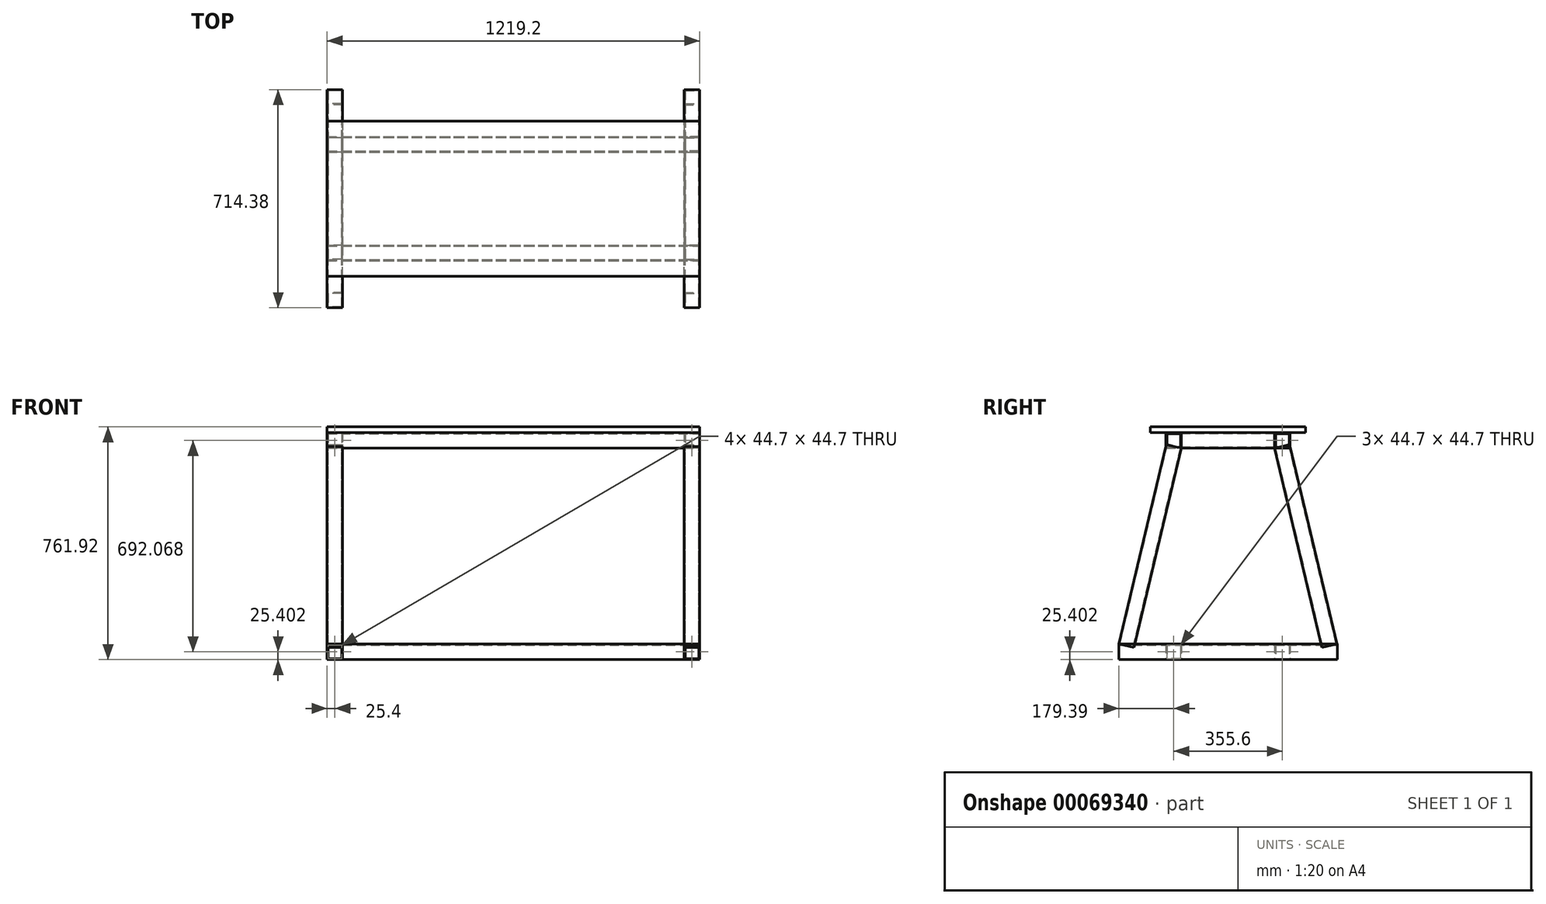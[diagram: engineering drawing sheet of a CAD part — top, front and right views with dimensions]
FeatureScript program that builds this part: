
annotation { "Feature Type Name" : "Feature", "Feature Type Description" : "" }
export const myFeature = defineFeature(function(context is Context, id is Id, definition is map)
    precondition{}
    {
        {
            var Q0;
            Q0=qCreatedBy(makeId("Top.planeOp"),FACE);
            var sketch = newSketch(context, id + "F0", { "sketchPlane" : qUnion([Q0])});
            skLineSegment(sketch, "E0.rect.bottom", {"start": v(-609.6, -254) * mm, "end": v(609.6, -254) * mm});
            skLineSegment(sketch, "E0.rect.top", {"start": v(-609.6, 254) * mm, "end": v(609.6, 254) * mm});
            skLineSegment(sketch, "E0.rect.left", {"start": v(-609.6, -254) * mm, "end": v(-609.6, 254) * mm});
            skLineSegment(sketch, "E0.rect.right", {"start": v(609.6, -254) * mm, "end": v(609.6, 254) * mm});
            skPoint(sketch, "E0.rect.middle", {"position": v(0, 0) * mm});
            skSolve(sketch);
        }
        {
            var Q0;
            Q0=makeQuery(id+"F0.imprint","IMPRINT",FACE,{"disambiguationData":[TD([[makeQuery(id+"F0.imprint","IMPRINT",EDGE,{"derivedFrom":sQuery(id+"F0.wireOp",EDGE,"E0.rect.bottom")}),1.0]])]});
            extrude(context, id + "F1", {"entities" : qUnion([Q0]), "depth" : 19.05 * mm});
        }
        {
            var Q0;
            Q0=makeQuery(id+"F1.opExtrude","SWEPT_FACE",FACE,{"disambiguationData":[OSD([sQuery(id+"F0.wireOp",EDGE,"E0.rect.right")])]});
            var Q1;
            Q1=makeQuery(id+"F1.opExtrude","SWEPT_FACE",FACE,{"disambiguationData":[OSD([sQuery(id+"F0.wireOp",EDGE,"E0.rect.right")])]});
            var sketch = newSketch(context, id + "F2", { "sketchPlane" : qUnion([Q0, Q1])});
            skPoint(sketch, "E1", {"position": v(-177.8, -25.4) * mm});
            skLineSegment(sketch, "E2.rect.bottom", {"start": v(-203.2, 0) * mm, "end": v(-152.4, 0) * mm});
            skLineSegment(sketch, "E2.rect.top", {"start": v(-203.2, -50.8) * mm, "end": v(-152.4, -50.8) * mm});
            skLineSegment(sketch, "E2.rect.right", {"start": v(-152.4, 0) * mm, "end": v(-152.4, -50.8) * mm});
            skLineSegment(sketch, "E3.rect.bottom", {"start": v(-200.15, -3.05) * mm, "end": v(-155.45, -3.05) * mm});
            skLineSegment(sketch, "E3.rect.top", {"start": v(-200.15, -47.75) * mm, "end": v(-155.45, -47.75) * mm});
            skLineSegment(sketch, "E3.rect.left", {"start": v(-200.15, -3.05) * mm, "end": v(-200.15, -47.75) * mm});
            skLineSegment(sketch, "E3.rect.right", {"start": v(-155.45, -3.05) * mm, "end": v(-155.45, -47.75) * mm});
            skLineSegment(sketch, "E4", {"start": v(0, 0) * mm, "end": v(0, -111.65) * mm});
            skLineSegment(sketch, "E5", {"start": v(-203.2, 0) * mm, "end": v(-203.2, -50.8) * mm});
            skPoint(sketch, "E6.MirrorP", {"position": v(177.8, -25.4) * mm});
            skLineSegment(sketch, "E7.MirrorCS", {"start": v(203.2, 0) * mm, "end": v(152.4, 0) * mm});
            skLineSegment(sketch, "E8.MirrorCS", {"start": v(155.45, -3.05) * mm, "end": v(155.45, -47.75) * mm});
            skLineSegment(sketch, "E9.MirrorCS", {"start": v(200.15, -3.05) * mm, "end": v(200.15, -47.75) * mm});
            skLineSegment(sketch, "E10.MirrorCS", {"start": v(203.2, 0) * mm, "end": v(203.2, -50.8) * mm});
            skLineSegment(sketch, "E11.MirrorCS", {"start": v(200.15, -47.75) * mm, "end": v(155.45, -47.75) * mm});
            skLineSegment(sketch, "E12.MirrorCS", {"start": v(200.15, -3.05) * mm, "end": v(155.45, -3.05) * mm});
            skLineSegment(sketch, "E13.MirrorCS", {"start": v(152.4, 0) * mm, "end": v(152.4, -50.8) * mm});
            skLineSegment(sketch, "E14.MirrorCS", {"start": v(203.2, -50.8) * mm, "end": v(152.4, -50.8) * mm});
            skSolve(sketch);
        }
        {
            var Q0;
            Q0=makeQuery(id+"F2.imprint","IMPRINT",FACE,{"disambiguationData":[TD([[makeQuery(id+"F2.imprint","IMPRINT",EDGE,{"derivedFrom":sQuery(id+"F2.wireOp",EDGE,"E7.MirrorCS")}),-1.0]])]});
            var Q1;
            Q1=makeQuery(id+"F2.imprint","IMPRINT",FACE,{"disambiguationData":[TD([[makeQuery(id+"F2.imprint","IMPRINT",EDGE,{"derivedFrom":sQuery(id+"F2.wireOp",EDGE,"E2.rect.bottom")}),-1.0]])]});
            extrude(context, id + "F3", {"entities" : qUnion([Q0, Q1]), "oppositeDirection" : true, "depth" : 1219.2 * mm});
        }
        {
            var Q0;
            Q0=makeQuery(id+"F3.opExtrude","SWEPT_FACE",FACE,{"disambiguationData":[OSD([sQuery(id+"F2.wireOp",EDGE,"E2.rect.right")])]});
            var sketch = newSketch(context, id + "F4", { "sketchPlane" : qUnion([Q0])});
            skLineSegment(sketch, "E15.rect.bottom", {"start": v(-609.6, 0) * mm, "end": v(-558.8, 0) * mm});
            skLineSegment(sketch, "E15.rect.top", {"start": v(-609.6, -50.8) * mm, "end": v(-558.8, -50.8) * mm});
            skLineSegment(sketch, "E15.rect.left", {"start": v(-609.6, 0) * mm, "end": v(-609.6, -50.8) * mm});
            skLineSegment(sketch, "E15.rect.right", {"start": v(-558.8, 0) * mm, "end": v(-558.8, -50.8) * mm});
            skPoint(sketch, "E15.rect.middle", {"position": v(-584.2, -25.4) * mm});
            skLineSegment(sketch, "E16.rect.bottom", {"start": v(-606.55, -3.05) * mm, "end": v(-561.85, -3.05) * mm});
            skLineSegment(sketch, "E16.rect.top", {"start": v(-606.55, -47.75) * mm, "end": v(-561.85, -47.75) * mm});
            skLineSegment(sketch, "E16.rect.left", {"start": v(-606.55, -3.05) * mm, "end": v(-606.55, -47.75) * mm});
            skLineSegment(sketch, "E16.rect.right", {"start": v(-561.85, -3.05) * mm, "end": v(-561.85, -47.75) * mm});
            skPoint(sketch, "E17.MirrorP", {"position": v(584.2, -25.4) * mm});
            skLineSegment(sketch, "E18.MirrorCS", {"start": v(561.85, -3.05) * mm, "end": v(561.85, -47.75) * mm});
            skLineSegment(sketch, "E19.MirrorCS", {"start": v(606.55, -3.05) * mm, "end": v(606.55, -47.75) * mm});
            skLineSegment(sketch, "E20.MirrorCS", {"start": v(606.55, -47.75) * mm, "end": v(561.85, -47.75) * mm});
            skLineSegment(sketch, "E21.MirrorCS", {"start": v(606.55, -3.05) * mm, "end": v(561.85, -3.05) * mm});
            skLineSegment(sketch, "E22.MirrorCS", {"start": v(609.6, 0) * mm, "end": v(609.6, -50.8) * mm});
            skLineSegment(sketch, "E23.MirrorCS", {"start": v(558.8, 0) * mm, "end": v(558.8, -50.8) * mm});
            skLineSegment(sketch, "E24.MirrorCS", {"start": v(609.6, -50.8) * mm, "end": v(558.8, -50.8) * mm});
            skLineSegment(sketch, "E25.MirrorCS", {"start": v(609.6, 0) * mm, "end": v(558.8, 0) * mm});
            skSolve(sketch);
        }
        {
            var Q0;
            Q0=makeQuery(id+"F4.imprint","IMPRINT",FACE,{"disambiguationData":[TD([[makeQuery(id+"F4.imprint","IMPRINT",EDGE,{"derivedFrom":sQuery(id+"F4.wireOp",EDGE,"E15.rect.bottom")}),1.0]])]});
            var Q1;
            Q1=makeQuery(id+"F4.imprint","IMPRINT",FACE,{"disambiguationData":[TD([[makeQuery(id+"F4.imprint","IMPRINT",EDGE,{"derivedFrom":sQuery(id+"F4.wireOp",EDGE,"E18.MirrorCS")}),-1.0]])]});
            extrude(context, id + "F5", {"entities" : qUnion([Q0, Q1]), "depth" : 304.8 * mm});
        }
        {
            var Q0;
            Q0=makeQuery(id+"F5.opExtrude","SWEPT_FACE",FACE,{"disambiguationData":[OSD([sQuery(id+"F4.wireOp",EDGE,"E15.rect.left")])]});
            var sketch = newSketch(context, id + "F6", { "sketchPlane" : qUnion([Q0])});
            skLineSegment(sketch, "E26", {"start": v(0, 0) * mm, "end": v(0, -692.15) * mm, "construction": true});
            skPoint(sketch, "E26.endSnap0", {"position": v(0, 0) * mm});
            skLineSegment(sketch, "E27", {"start": v(0, -50.8) * mm, "end": v(-177.8, -50.8) * mm, "construction": true});
            skLineSegment(sketch, "E28", {"start": v(0, -692.15) * mm, "end": v(-330.2, -692.15) * mm, "construction": true});
            skLineSegment(sketch, "E29", {"start": v(-177.8, -50.8) * mm, "end": v(-330.2, -692.15) * mm, "construction": true});
            skLineSegment(sketch, "E30", {"start": v(-177.8, -50.8) * mm, "end": v(0, -50.8) * mm, "construction": true});
            skLineSegment(sketch, "E31", {"start": v(-177.8, -50.8) * mm, "end": v(-177.8, -176.29) * mm, "construction": true});
            skLineSegment(sketch, "E32", {"start": v(-177.8, -176.29) * mm, "end": v(-206.02, -169.58) * mm, "construction": true});
            skLineSegment(sketch, "E33", {"start": v(-330.2, -692.15) * mm, "end": v(-489, -692.15) * mm, "construction": true});
            skSolve(sketch);
        }
        {
            var Q0;
            Q0=sQuery(id+"F6.wireOp",EDGE,"E32");
            cPlane(context, id + "F7", {"entities" : qUnion([Q0]), "cplaneType" : CPlaneType.LINE_ANGLE, "offset" : 152.4 * mm, "angle" : 0 * degree, "width" : 152.4 * mm, "height" : 152.4 * mm});
        }
        {
            var Q0;
            Q0=qCreatedBy(id+"F7.planeOp",FACE);
            cPlane(context, id + "F8", {"entities" : qUnion([Q0]), "cplaneType" : CPlaneType.OFFSET, "offset" : 127.96 * mm, "oppositeDirection" : true, "width" : 152.4 * mm, "height" : 152.4 * mm});
        }
        {
            var Q0;
            Q0=qCreatedBy(id+"F8.planeOp",FACE);
            var sketch = newSketch(context, id + "F9", { "sketchPlane" : qUnion([Q0])});
            skLineSegment(sketch, "E34", {"start": v(609.6, 136.53) * mm, "end": v(558.8, 136.53) * mm, "construction": true});
            skLineSegment(sketch, "E35", {"start": v(584.2, 136.53) * mm, "end": v(584.2, 204.32) * mm, "construction": true});
            skLineSegment(sketch, "E36", {"start": v(584.2, 161.93) * mm, "end": v(621.33, 161.93) * mm, "construction": true});
            skPoint(sketch, "E37", {"position": v(584.2, 161.93) * mm});
            skLineSegment(sketch, "E38.rect.bottom", {"start": v(558.8, 136.53) * mm, "end": v(609.6, 136.53) * mm});
            skLineSegment(sketch, "E38.rect.top", {"start": v(558.8, 187.33) * mm, "end": v(609.6, 187.33) * mm});
            skLineSegment(sketch, "E38.rect.left", {"start": v(558.8, 136.53) * mm, "end": v(558.8, 187.33) * mm});
            skLineSegment(sketch, "E38.rect.right", {"start": v(609.6, 136.53) * mm, "end": v(609.6, 187.33) * mm});
            skLineSegment(sketch, "E39.rect.bottom", {"start": v(561.85, 139.58) * mm, "end": v(606.55, 139.58) * mm});
            skLineSegment(sketch, "E39.rect.top", {"start": v(561.85, 184.28) * mm, "end": v(606.55, 184.28) * mm});
            skLineSegment(sketch, "E39.rect.left", {"start": v(561.85, 139.58) * mm, "end": v(561.85, 184.28) * mm});
            skLineSegment(sketch, "E39.rect.right", {"start": v(606.55, 139.58) * mm, "end": v(606.55, 184.28) * mm});
            skPoint(sketch, "E40.MirrorP", {"position": v(-584.2, 161.93) * mm});
            skLineSegment(sketch, "E41.MirrorCS", {"start": v(-609.6, 136.53) * mm, "end": v(-558.8, 136.53) * mm, "construction": true});
            skLineSegment(sketch, "E42.MirrorCS", {"start": v(-606.55, 139.58) * mm, "end": v(-606.55, 184.28) * mm});
            skLineSegment(sketch, "E43.MirrorCS", {"start": v(-561.85, 139.58) * mm, "end": v(-561.85, 184.28) * mm});
            skLineSegment(sketch, "E44.MirrorCS", {"start": v(-561.85, 184.28) * mm, "end": v(-606.55, 184.28) * mm});
            skLineSegment(sketch, "E45.MirrorCS", {"start": v(-558.8, 136.53) * mm, "end": v(-609.6, 136.53) * mm});
            skLineSegment(sketch, "E46.MirrorCS", {"start": v(-558.8, 187.33) * mm, "end": v(-609.6, 187.33) * mm});
            skLineSegment(sketch, "E47.MirrorCS", {"start": v(-609.6, 136.53) * mm, "end": v(-609.6, 187.33) * mm});
            skLineSegment(sketch, "E48.MirrorCS", {"start": v(-561.85, 139.58) * mm, "end": v(-606.55, 139.58) * mm});
            skLineSegment(sketch, "E49.MirrorCS", {"start": v(-558.8, 136.53) * mm, "end": v(-558.8, 187.33) * mm});
            skSolve(sketch);
        }
        {
            var Q0;
            Q0=makeQuery(id+"F9.imprint","IMPRINT",FACE,{"disambiguationData":[TD([[makeQuery(id+"F9.imprint","IMPRINT",EDGE,{"derivedFrom":sQuery(id+"F9.wireOp",EDGE,"E38.rect.bottom")}),1.0]])]});
            var Q1;
            Q1=makeQuery(id+"F9.imprint","IMPRINT",FACE,{"disambiguationData":[TD([[makeQuery(id+"F9.imprint","IMPRINT",EDGE,{"derivedFrom":sQuery(id+"F9.wireOp",EDGE,"E42.MirrorCS")}),1.0]])]});
            extrude(context, id + "F10", {"entities" : qUnion([Q0, Q1]), "operationType" : NewBodyOperationType.ADD, "depth" : 671.2 * mm});
        }
        {
            var Q0;
            Q0=makeQuery(id+"F3.opExtrude","SWEPT_BODY",BODY,{"disambiguationData":[OSD([sQuery(id+"F2.wireOp",EDGE,"E2.rect.bottom"),sQuery(id+"F2.wireOp",EDGE,"E2.rect.top"),sQuery(id+"F2.wireOp",EDGE,"E2.rect.right"),sQuery(id+"F2.wireOp",EDGE,"E3.rect.bottom"),sQuery(id+"F2.wireOp",EDGE,"E3.rect.top"),sQuery(id+"F2.wireOp",EDGE,"E3.rect.left"),sQuery(id+"F2.wireOp",EDGE,"E3.rect.right"),sQuery(id+"F2.wireOp",EDGE,"E5")])]});
            var Q1;
            Q1=qCreatedBy(makeId("Front.planeOp"),FACE);
            mirror(context, id + "F11", {"entities" : qUnion([Q0]), "mirrorPlane" : qUnion([Q1])});
        }
        {
            var Q0;
            Q0=qCreatedBy(makeId("Front.planeOp"),FACE);
            var sketch = newSketch(context, id + "F12", { "sketchPlane" : qUnion([Q0])});
            skLineSegment(sketch, "E50.bottom", {"start": v(609.6, -692.07) * mm, "end": v(558.8, -692.07) * mm});
            skLineSegment(sketch, "E50.top", {"start": v(609.6, -742.87) * mm, "end": v(558.8, -742.87) * mm});
            skLineSegment(sketch, "E50.left", {"start": v(609.6, -692.07) * mm, "end": v(609.6, -742.87) * mm});
            skLineSegment(sketch, "E50.right", {"start": v(558.8, -692.07) * mm, "end": v(558.8, -742.87) * mm});
            skLineSegment(sketch, "E51.bottom", {"start": v(561.85, -739.82) * mm, "end": v(606.55, -739.82) * mm});
            skLineSegment(sketch, "E51.top", {"start": v(561.85, -695.12) * mm, "end": v(606.55, -695.12) * mm});
            skLineSegment(sketch, "E51.left", {"start": v(561.85, -739.82) * mm, "end": v(561.85, -695.12) * mm});
            skLineSegment(sketch, "E51.right", {"start": v(606.55, -739.82) * mm, "end": v(606.55, -695.12) * mm});
            skLineSegment(sketch, "E52.MirrorCS", {"start": v(-558.8, -692.07) * mm, "end": v(-558.8, -742.87) * mm});
            skLineSegment(sketch, "E53.MirrorCS", {"start": v(-609.6, -692.07) * mm, "end": v(-558.8, -692.07) * mm});
            skLineSegment(sketch, "E54.MirrorCS", {"start": v(-606.55, -739.82) * mm, "end": v(-606.55, -695.12) * mm});
            skLineSegment(sketch, "E55.MirrorCS", {"start": v(-561.85, -739.82) * mm, "end": v(-561.85, -695.12) * mm});
            skLineSegment(sketch, "E56.MirrorCS", {"start": v(-561.85, -695.12) * mm, "end": v(-606.55, -695.12) * mm});
            skLineSegment(sketch, "E57.MirrorCS", {"start": v(-609.6, -742.87) * mm, "end": v(-558.8, -742.87) * mm});
            skLineSegment(sketch, "E58.MirrorCS", {"start": v(-609.6, -692.07) * mm, "end": v(-609.6, -742.87) * mm});
            skLineSegment(sketch, "E59.MirrorCS", {"start": v(-561.85, -739.82) * mm, "end": v(-606.55, -739.82) * mm});
            skSolve(sketch);
        }
        {
            var Q0;
            Q0=makeQuery(id+"F12.imprint","IMPRINT",FACE,{"disambiguationData":[TD([[makeQuery(id+"F12.imprint","IMPRINT",EDGE,{"derivedFrom":sQuery(id+"F12.wireOp",EDGE,"E50.bottom")}),1.0]])]});
            var Q1;
            Q1=makeQuery(id+"F12.imprint","IMPRINT",FACE,{"disambiguationData":[TD([[makeQuery(id+"F12.imprint","IMPRINT",EDGE,{"derivedFrom":sQuery(id+"F12.wireOp",EDGE,"E52.MirrorCS")}),-1.0]])]});
            extrude(context, id + "F13", {"entities" : qUnion([Q0, Q1]), "endBound" : BoundingType.SYMMETRIC, "depth" : 714.38 * mm});
        }
        {
            var Q0;
            Q0=makeQuery(id+"F5.opExtrude","SWEPT_FACE",FACE,{"disambiguationData":[OSD([sQuery(id+"F4.wireOp",EDGE,"E15.rect.right")])]});
            var sketch = newSketch(context, id + "F14", { "sketchPlane" : qUnion([Q0])});
            skLineSegment(sketch, "E60", {"start": v(152.4, -50.8) * mm, "end": v(331.27, -50.35) * mm, "construction": true});
            skLineSegment(sketch, "E61.bottom", {"start": v(152.4, -692.07) * mm, "end": v(203.2, -692.07) * mm});
            skLineSegment(sketch, "E61.top", {"start": v(152.4, -742.87) * mm, "end": v(203.2, -742.87) * mm});
            skLineSegment(sketch, "E61.left", {"start": v(152.4, -692.07) * mm, "end": v(152.4, -742.87) * mm});
            skLineSegment(sketch, "E61.right", {"start": v(203.2, -692.07) * mm, "end": v(203.2, -742.87) * mm});
            skLineSegment(sketch, "E62", {"start": v(152.4, 0) * mm, "end": v(152.4, -763.8) * mm, "construction": true});
            skLineSegment(sketch, "E63.bottom", {"start": v(155.45, -695.12) * mm, "end": v(200.15, -695.12) * mm});
            skLineSegment(sketch, "E63.top", {"start": v(155.45, -739.82) * mm, "end": v(200.15, -739.82) * mm});
            skLineSegment(sketch, "E63.left", {"start": v(155.45, -695.12) * mm, "end": v(155.45, -739.82) * mm});
            skLineSegment(sketch, "E63.right", {"start": v(200.15, -695.12) * mm, "end": v(200.15, -739.82) * mm});
            skLineSegment(sketch, "E64.MirrorCS", {"start": v(-200.15, -695.12) * mm, "end": v(-200.15, -739.82) * mm});
            skLineSegment(sketch, "E65.MirrorCS", {"start": v(-155.45, -695.12) * mm, "end": v(-155.45, -739.82) * mm});
            skLineSegment(sketch, "E66.MirrorCS", {"start": v(-155.45, -739.82) * mm, "end": v(-200.15, -739.82) * mm});
            skLineSegment(sketch, "E67.MirrorCS", {"start": v(-152.4, 0) * mm, "end": v(-152.4, -763.8) * mm, "construction": true});
            skLineSegment(sketch, "E68.MirrorCS", {"start": v(-152.4, -692.07) * mm, "end": v(-203.2, -692.07) * mm});
            skLineSegment(sketch, "E69.MirrorCS", {"start": v(-152.4, -742.87) * mm, "end": v(-203.2, -742.87) * mm});
            skLineSegment(sketch, "E70.MirrorCS", {"start": v(-155.45, -695.12) * mm, "end": v(-200.15, -695.12) * mm});
            skLineSegment(sketch, "E71.MirrorCS", {"start": v(-203.2, -692.07) * mm, "end": v(-203.2, -742.87) * mm});
            skLineSegment(sketch, "E72.MirrorCS", {"start": v(-152.4, -692.07) * mm, "end": v(-152.4, -742.87) * mm});
            skSolve(sketch);
        }
        {
            var Q0;
            Q0=makeQuery(id+"F14.imprint","IMPRINT",FACE,{"disambiguationData":[TD([[makeQuery(id+"F14.imprint","IMPRINT",EDGE,{"derivedFrom":sQuery(id+"F14.wireOp",EDGE,"E64.MirrorCS")}),-1.0]])]});
            var Q1;
            Q1=makeQuery(id+"F14.imprint","IMPRINT",FACE,{"disambiguationData":[TD([[makeQuery(id+"F14.imprint","IMPRINT",EDGE,{"derivedFrom":sQuery(id+"F14.wireOp",EDGE,"E61.bottom")}),-1.0]])]});
            extrude(context, id + "F15", {"entities" : qUnion([Q0, Q1]), "depth" : 1117.6 * mm});
        }
    });
